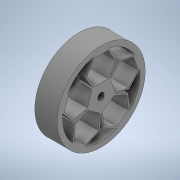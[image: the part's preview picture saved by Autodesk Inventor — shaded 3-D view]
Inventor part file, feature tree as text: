
AUTODESK INVENTOR PART (.ipt)
format: ipt  version: 2020 (Build 240168000, 168)  size: 391,168 bytes
history: native  units: in
note: dims shown in document units (in); Inventor stores cm internally (conversion verified against a paired STEP export)
features: extrude x1, sketch x1
ambient origin geometry x8: Origin, YZ Plane, XZ Plane, XY Plane, X Axis, Y Axis, Z Axis, Center Point
bodies: Solid1 (feature_tree)
feature tree (2):
  extrude  "Extrusion2"  Depth=0.0315in
  sketch  "Sketch2"  dims[d10=0.1181in d11=0.0315in d16=0.5in d17=0.0in d29=1.9685in d31=360.0deg d33=0.1575in d34=0.0591in d35=0.5906in d36=1.9685in]
